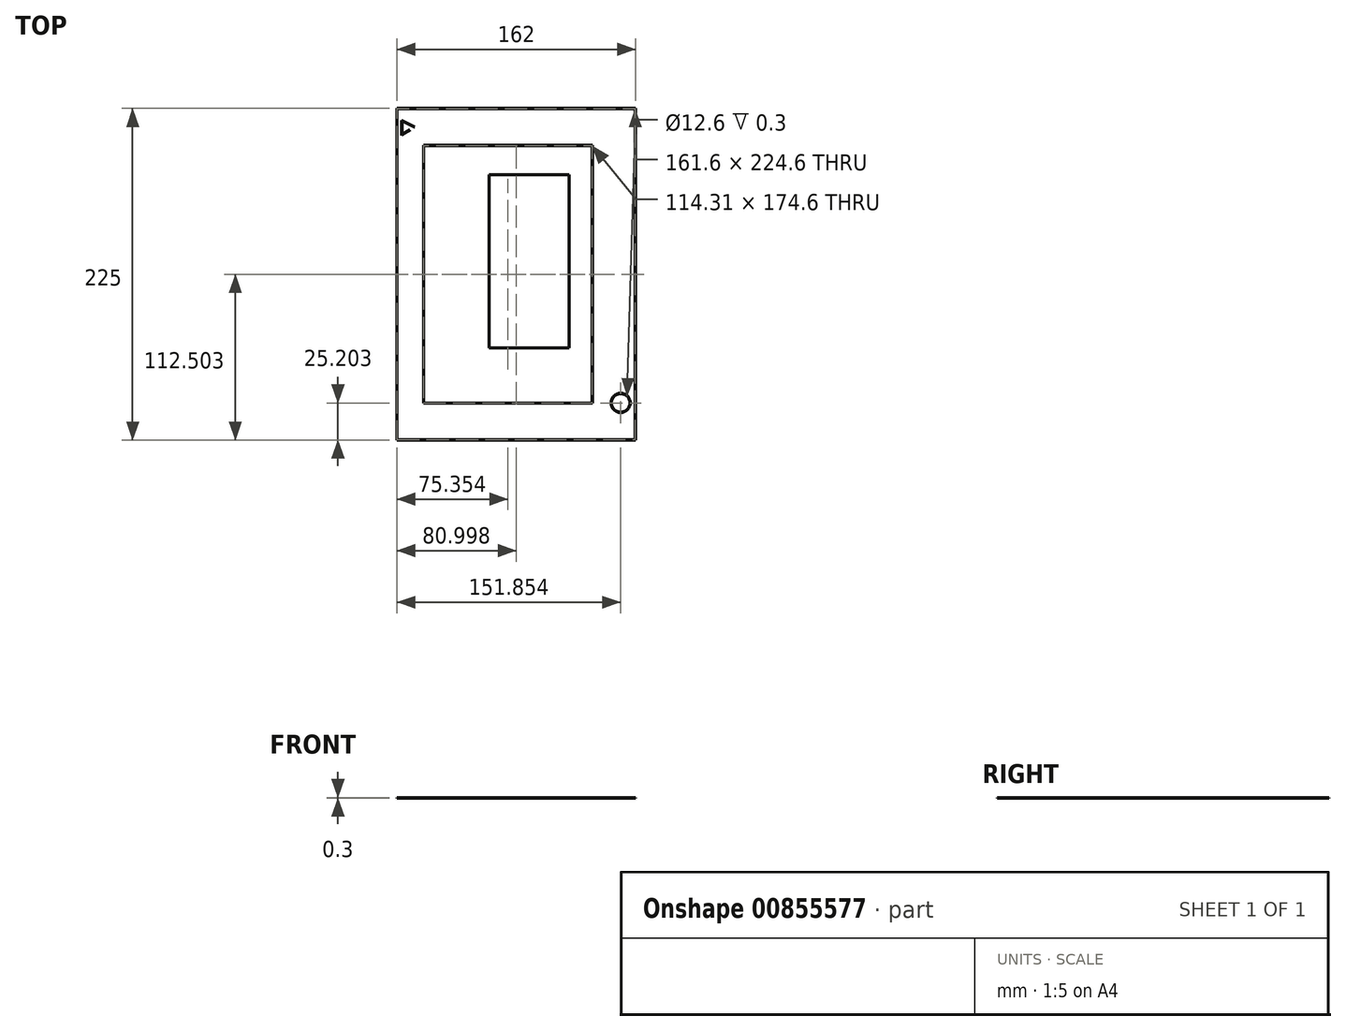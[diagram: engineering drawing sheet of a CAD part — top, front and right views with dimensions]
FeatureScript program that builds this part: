
annotation { "Feature Type Name" : "Feature", "Feature Type Description" : "" }
export const myFeature = defineFeature(function(context is Context, id is Id, definition is map)
    precondition{}
    {
        {
            assignVariable(context, id + "F0", {"name" : "LineHeight", "anyValue" : 0.3});
        }
        {
            var Q0;
            Q0=qCreatedBy(makeId("Top.planeOp"),FACE);
            var sketch = newSketch(context, id + "F1", { "sketchPlane" : qUnion([Q0])});
            skLineSegment(sketch, "E0.bottom", {"start": v(-91.48, 152.86) * mm, "end": v(70.52, 152.86) * mm});
            skLineSegment(sketch, "E0.top", {"start": v(-91.48, -72.14) * mm, "end": v(70.52, -72.14) * mm});
            skLineSegment(sketch, "E0.left", {"start": v(-91.48, 152.86) * mm, "end": v(-91.48, -72.14) * mm});
            skLineSegment(sketch, "E0.right", {"start": v(70.52, 152.86) * mm, "end": v(70.52, -72.14) * mm});
            skLineSegment(sketch, "E1.bottom", {"start": v(-82.48, 140.36) * mm, "end": v(50.23, 140.36) * mm});
            skLineSegment(sketch, "E1.top", {"start": v(-82.48, -59.64) * mm, "end": v(50.23, -59.64) * mm});
            skLineSegment(sketch, "E1.left", {"start": v(-82.48, 140.36) * mm, "end": v(-82.48, -59.64) * mm});
            skLineSegment(sketch, "E1.right", {"start": v(50.23, 140.36) * mm, "end": v(50.23, -59.64) * mm});
            skLineSegment(sketch, "E2.bottom", {"start": v(-73.48, 127.86) * mm, "end": v(41.23, 127.86) * mm});
            skLineSegment(sketch, "E2.top", {"start": v(-73.48, -47.14) * mm, "end": v(41.23, -47.14) * mm});
            skLineSegment(sketch, "E2.left", {"start": v(-73.48, 127.86) * mm, "end": v(-73.48, -47.14) * mm});
            skLineSegment(sketch, "E2.right", {"start": v(41.23, 127.86) * mm, "end": v(41.23, -47.14) * mm});
            skLineSegment(sketch, "E3.bottom", {"start": v(-28.98, 107.86) * mm, "end": v(25.52, 107.86) * mm});
            skLineSegment(sketch, "E3.top", {"start": v(-28.98, -9.64) * mm, "end": v(25.52, -9.64) * mm});
            skLineSegment(sketch, "E3.left", {"start": v(-28.98, 107.86) * mm, "end": v(-28.98, -9.64) * mm});
            skLineSegment(sketch, "E3.right", {"start": v(25.52, 107.86) * mm, "end": v(25.52, -9.64) * mm});
            skLineSegment(sketch, "E4", {"start": v(-88.28, 144.66) * mm, "end": v(-88.28, 134.66) * mm});
            skLineSegment(sketch, "E5", {"start": v(-88.28, 134.66) * mm, "end": v(-79.35, 140.16) * mm});
            skLineSegment(sketch, "E6", {"start": v(-79.35, 140.16) * mm, "end": v(-88.28, 144.66) * mm});
            skCircle(sketch, "E7", {"center": v(60.37, -46.94) * mm, "radius": 6.5 * mm});
            skLineSegment(sketch, "E8", {"start": v(50.23, -46.94) * mm, "end": v(70.52, -46.94) * mm, "construction": true});
            skLineSegment(sketch, "E9", {"start": v(-91.28, 152.66) * mm, "end": v(70.32, 152.66) * mm});
            skLineSegment(sketch, "E10", {"start": v(70.32, 152.66) * mm, "end": v(70.32, -71.94) * mm});
            skLineSegment(sketch, "E11", {"start": v(70.32, -71.94) * mm, "end": v(-91.28, -71.94) * mm});
            skLineSegment(sketch, "E12", {"start": v(-91.28, -71.94) * mm, "end": v(-91.28, 152.66) * mm});
            skLineSegment(sketch, "E13", {"start": v(-82.28, 140.16) * mm, "end": v(50.03, 140.16) * mm});
            skLineSegment(sketch, "E14", {"start": v(50.03, 140.16) * mm, "end": v(50.03, -59.44) * mm});
            skLineSegment(sketch, "E15", {"start": v(50.03, -59.44) * mm, "end": v(-82.28, -59.44) * mm});
            skLineSegment(sketch, "E16", {"start": v(-82.28, -59.44) * mm, "end": v(-82.28, 140.16) * mm});
            skLineSegment(sketch, "E17", {"start": v(-73.28, 127.66) * mm, "end": v(41.03, 127.66) * mm});
            skLineSegment(sketch, "E18", {"start": v(41.03, 127.66) * mm, "end": v(41.03, -46.94) * mm});
            skLineSegment(sketch, "E19", {"start": v(41.03, -46.94) * mm, "end": v(-73.28, -46.94) * mm});
            skLineSegment(sketch, "E20", {"start": v(-73.28, -46.94) * mm, "end": v(-73.28, 127.66) * mm});
            skCircle(sketch, "E21", {"center": v(60.37, -46.94) * mm, "radius": 6.3 * mm});
            skLineSegment(sketch, "E22", {"start": v(-88.08, 144.34) * mm, "end": v(-79.76, 140.15) * mm});
            skPoint(sketch, "E22.startSnap0", {"position": v(-86.01, 144.34) * mm});
            skLineSegment(sketch, "E23", {"start": v(-79.76, 140.15) * mm, "end": v(-88.08, 135.02) * mm});
            skLineSegment(sketch, "E24", {"start": v(-88.08, 135.02) * mm, "end": v(-88.08, 144.34) * mm});
            skSolve(sketch);
        }
        {
            var Q0;
            Q0=makeQuery(id+"F1.imprint","IMPRINT",FACE,{"disambiguationData":[TD([[makeQuery(id+"F1.imprint","IMPRINT",EDGE,{"derivedFrom":sQuery(id+"F1.wireOp",EDGE,"E0.bottom")}),-1.0]])]});
            var Q1;
            Q1=makeQuery(id+"F1.imprint","IMPRINT",FACE,{"disambiguationData":[TD([[makeQuery(id+"F1.imprint","IMPRINT",EDGE,{"derivedFrom":sQuery(id+"F1.wireOp",EDGE,"E1.bottom")}),-1.0]])]});
            var Q2;
            Q2=makeQuery(id+"F1.imprint","IMPRINT",FACE,{"disambiguationData":[TD([[makeQuery(id+"F1.imprint","IMPRINT",EDGE,{"derivedFrom":sQuery(id+"F1.wireOp",EDGE,"E2.bottom")}),-1.0]])]});
            var Q3;
            Q3=makeQuery(id+"F1.imprint","IMPRINT",FACE,{"disambiguationData":[TD([[makeQuery(id+"F1.imprint","IMPRINT",EDGE,{"derivedFrom":sQuery(id+"F1.wireOp",EDGE,"E7")}),1.0]])]});
            var Q4;
            Q4=makeQuery(id+"F1.imprint","IMPRINT",FACE,{"disambiguationData":[TD([[makeQuery(id+"F1.imprint","IMPRINT",EDGE,{"derivedFrom":sQuery(id+"F1.wireOp",EDGE,"E3.bottom")}),-1.0]])]});
            var Q5;
            Q5=makeQuery(id+"F1.imprint","IMPRINT",FACE,{"disambiguationData":[TD([[makeQuery(id+"F1.imprint","IMPRINT",EDGE,{"derivedFrom":sQuery(id+"F1.wireOp",EDGE,"E4")}),1.0]])]});
            extrude(context, id + "F2", {"entities" : qUnion([Q0, Q1, Q2, Q3, Q4, Q5]), "depth" : (getVariable(context, 'LineHeight')) * mm, "offsetDistance" : 25 * mm});
        }
    });
